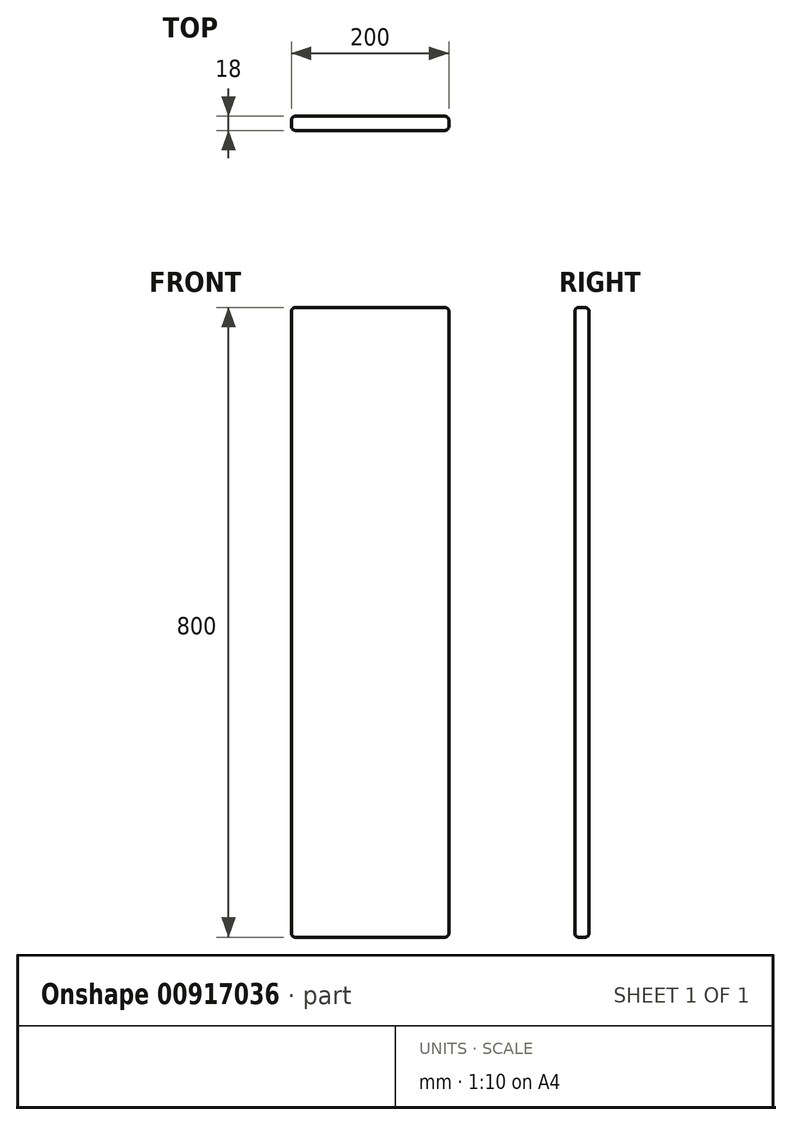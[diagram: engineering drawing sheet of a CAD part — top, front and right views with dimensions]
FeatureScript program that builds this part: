
annotation { "Feature Type Name" : "Feature", "Feature Type Description" : "" }
export const myFeature = defineFeature(function(context is Context, id is Id, definition is map)
    precondition{}
    {
        {
            var Q0;
            Q0=qCreatedBy(makeId("Front.planeOp"),FACE);
            var sketch = newSketch(context, id + "F0", { "sketchPlane" : qUnion([Q0])});
            skLineSegment(sketch, "E0.bottom", {"start": v(0, -230.64) * mm, "end": v(-200, -230.64) * mm});
            skLineSegment(sketch, "E0.top", {"start": v(0, 569.36) * mm, "end": v(-200, 569.36) * mm});
            skLineSegment(sketch, "E0.left", {"start": v(0, -230.64) * mm, "end": v(0, 569.36) * mm});
            skLineSegment(sketch, "E0.right", {"start": v(-200, -230.64) * mm, "end": v(-200, 569.36) * mm});
            skSolve(sketch);
        }
        {
            var Q0;
            Q0 = qSketchRegion(id + "F0", true);
            extrude(context, id + "F1", {"entities" : qUnion([Q0]), "depth" : 18 * mm, "offsetDistance" : 25.4 * mm});
        }
        {
            var Q0;
            Q0=makeQuery(id+"F1.opExtrude","CAP_EDGE",EDGE,{"disambiguationData":[OSD([sQuery(id+"F0.wireOp",EDGE,"E0.right")])],"isStart":false});
            var Q1;
            Q1=makeQuery(id+"F1.opExtrude","CAP_EDGE",EDGE,{"disambiguationData":[OSD([sQuery(id+"F0.wireOp",EDGE,"E0.right")])],"isStart":true});
            var Q2;
            Q2=makeQuery(id+"F1.opExtrude","CAP_EDGE",EDGE,{"disambiguationData":[OSD([sQuery(id+"F0.wireOp",EDGE,"E0.bottom")])],"isStart":false});
            var Q3;
            Q3=makeQuery(id+"F1.opExtrude","CAP_EDGE",EDGE,{"disambiguationData":[OSD([sQuery(id+"F0.wireOp",EDGE,"E0.bottom")])],"isStart":true});
            var Q4;
            Q4=makeQuery(id+"F1.opExtrude","CAP_EDGE",EDGE,{"disambiguationData":[OSD([sQuery(id+"F0.wireOp",EDGE,"E0.left")])],"isStart":false});
            var Q5;
            Q5=makeQuery(id+"F1.opExtrude","SWEPT_EDGE",EDGE,{"disambiguationData":[OSD([sQuery(id+"F0.wireOp",EDGE,"E0.bottom"),sQuery(id+"F0.wireOp",EDGE,"E0.right")])]});
            var Q6;
            Q6=makeQuery(id+"F1.opExtrude","SWEPT_EDGE",EDGE,{"disambiguationData":[OSD([sQuery(id+"F0.wireOp",EDGE,"E0.bottom"),sQuery(id+"F0.wireOp",EDGE,"E0.left")])]});
            var Q7;
            Q7=makeQuery(id+"F1.opExtrude","SWEPT_EDGE",EDGE,{"disambiguationData":[OSD([sQuery(id+"F0.wireOp",EDGE,"E0.top"),sQuery(id+"F0.wireOp",EDGE,"E0.right")])]});
            var Q8;
            Q8=makeQuery(id+"F1.opExtrude","CAP_EDGE",EDGE,{"disambiguationData":[OSD([sQuery(id+"F0.wireOp",EDGE,"E0.top")])],"isStart":false});
            var Q9;
            Q9=makeQuery(id+"F1.opExtrude","CAP_EDGE",EDGE,{"disambiguationData":[OSD([sQuery(id+"F0.wireOp",EDGE,"E0.top")])],"isStart":true});
            var Q10;
            Q10=makeQuery(id+"F1.opExtrude","CAP_EDGE",EDGE,{"disambiguationData":[OSD([sQuery(id+"F0.wireOp",EDGE,"E0.left")])],"isStart":true});
            fillet(context, id + "F2", {"entities" : qUnion([Q0, Q1, Q2, Q3, Q4, Q5, Q6, Q7, Q8, Q9, Q10]), "radius" : 5 * mm, "tangentPropagation" : true, "allowEdgeOverflow" : false});
        }
        {
            var Q0;
            Q0=makeQuery(id+"F1.opExtrude","SWEPT_EDGE",EDGE,{"disambiguationData":[OSD([sQuery(id+"F0.wireOp",EDGE,"E0.top"),sQuery(id+"F0.wireOp",EDGE,"E0.left")])]});
            fillet(context, id + "F3", {"entities" : qUnion([Q0]), "radius" : 5 * mm, "tangentPropagation" : true, "allowEdgeOverflow" : false});
        }
    });
